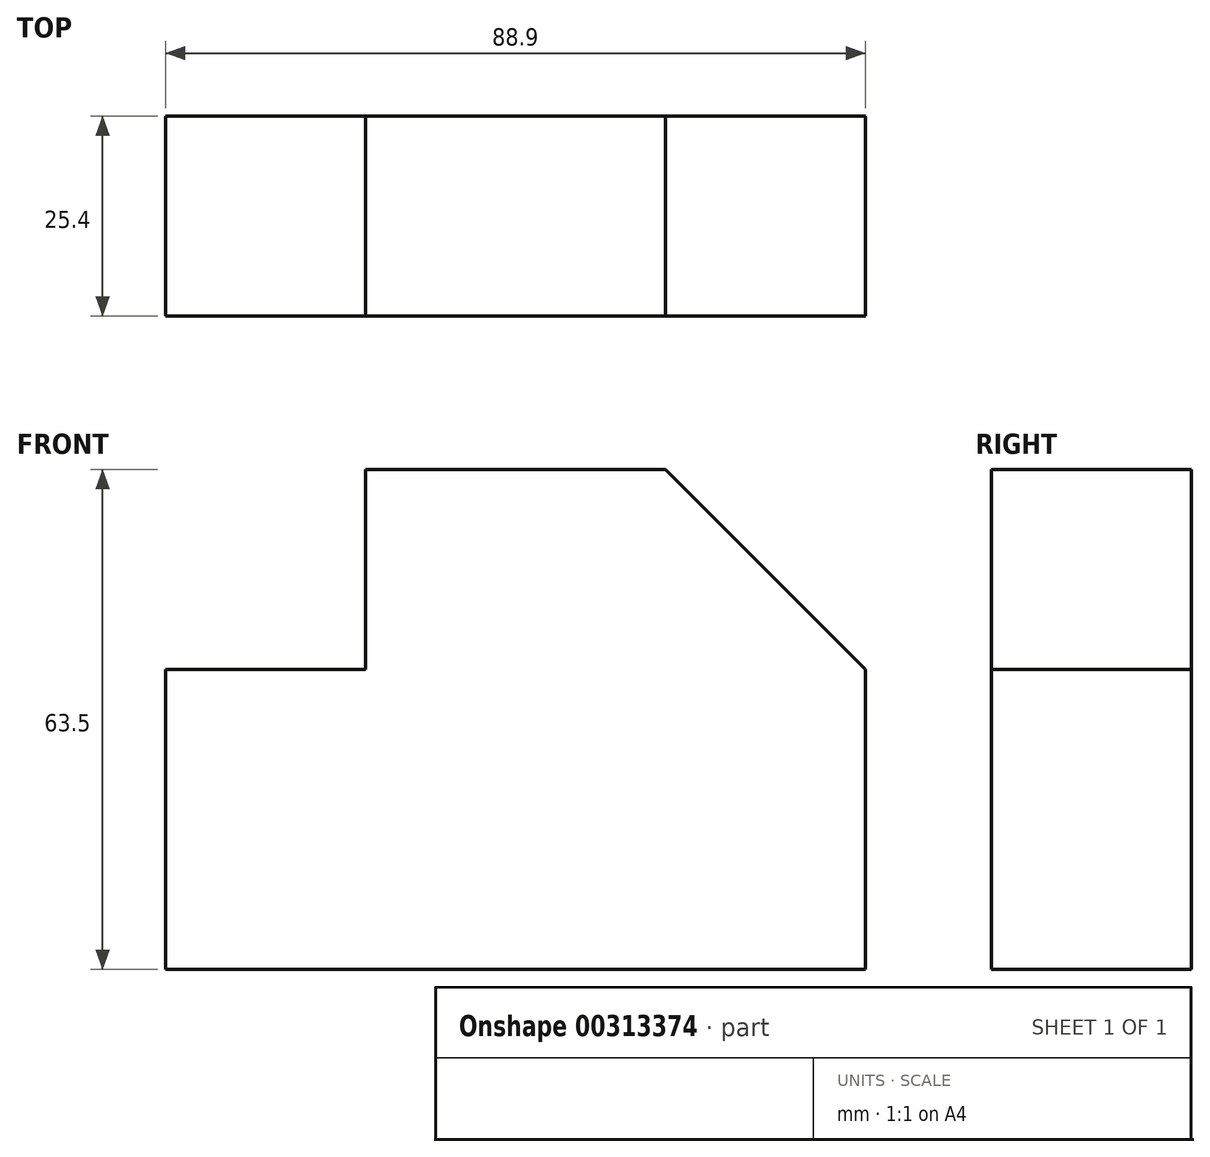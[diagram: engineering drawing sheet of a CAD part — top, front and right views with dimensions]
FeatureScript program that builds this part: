
annotation { "Feature Type Name" : "Feature", "Feature Type Description" : "" }
export const myFeature = defineFeature(function(context is Context, id is Id, definition is map)
    precondition{}
    {
        {
            var Q0;
            Q0=qCreatedBy(makeId("Front.planeOp"),FACE);
            var sketch = newSketch(context, id + "F0", { "sketchPlane" : qUnion([Q0])});
            skLineSegment(sketch, "E0", {"start": v(-55.14, -52.5) * mm, "end": v(33.76, -52.5) * mm});
            skLineSegment(sketch, "E1", {"start": v(-55.14, -52.5) * mm, "end": v(-55.14, -14.4) * mm});
            skLineSegment(sketch, "E2", {"start": v(-55.14, -14.4) * mm, "end": v(-29.74, -14.4) * mm});
            skLineSegment(sketch, "E3", {"start": v(-29.74, -14.4) * mm, "end": v(-29.74, 11) * mm});
            skLineSegment(sketch, "E4", {"start": v(-29.74, 11) * mm, "end": v(8.36, 11) * mm});
            skLineSegment(sketch, "E5", {"start": v(33.76, -52.5) * mm, "end": v(33.76, -14.4) * mm});
            skLineSegment(sketch, "E6", {"start": v(8.36, 11) * mm, "end": v(33.76, -14.4) * mm});
            skSolve(sketch);
        }
        {
            var Q0;
            Q0=makeQuery(id+"F0.imprint","IMPRINT",FACE,{"disambiguationData":[TD([[makeQuery(id+"F0.imprint","IMPRINT",EDGE,{"derivedFrom":sQuery(id+"F0.wireOp",EDGE,"E0")}),1.0]])]});
            extrude(context, id + "F1", {"entities" : qUnion([Q0]), "depth" : 25.4 * mm});
        }
    });
